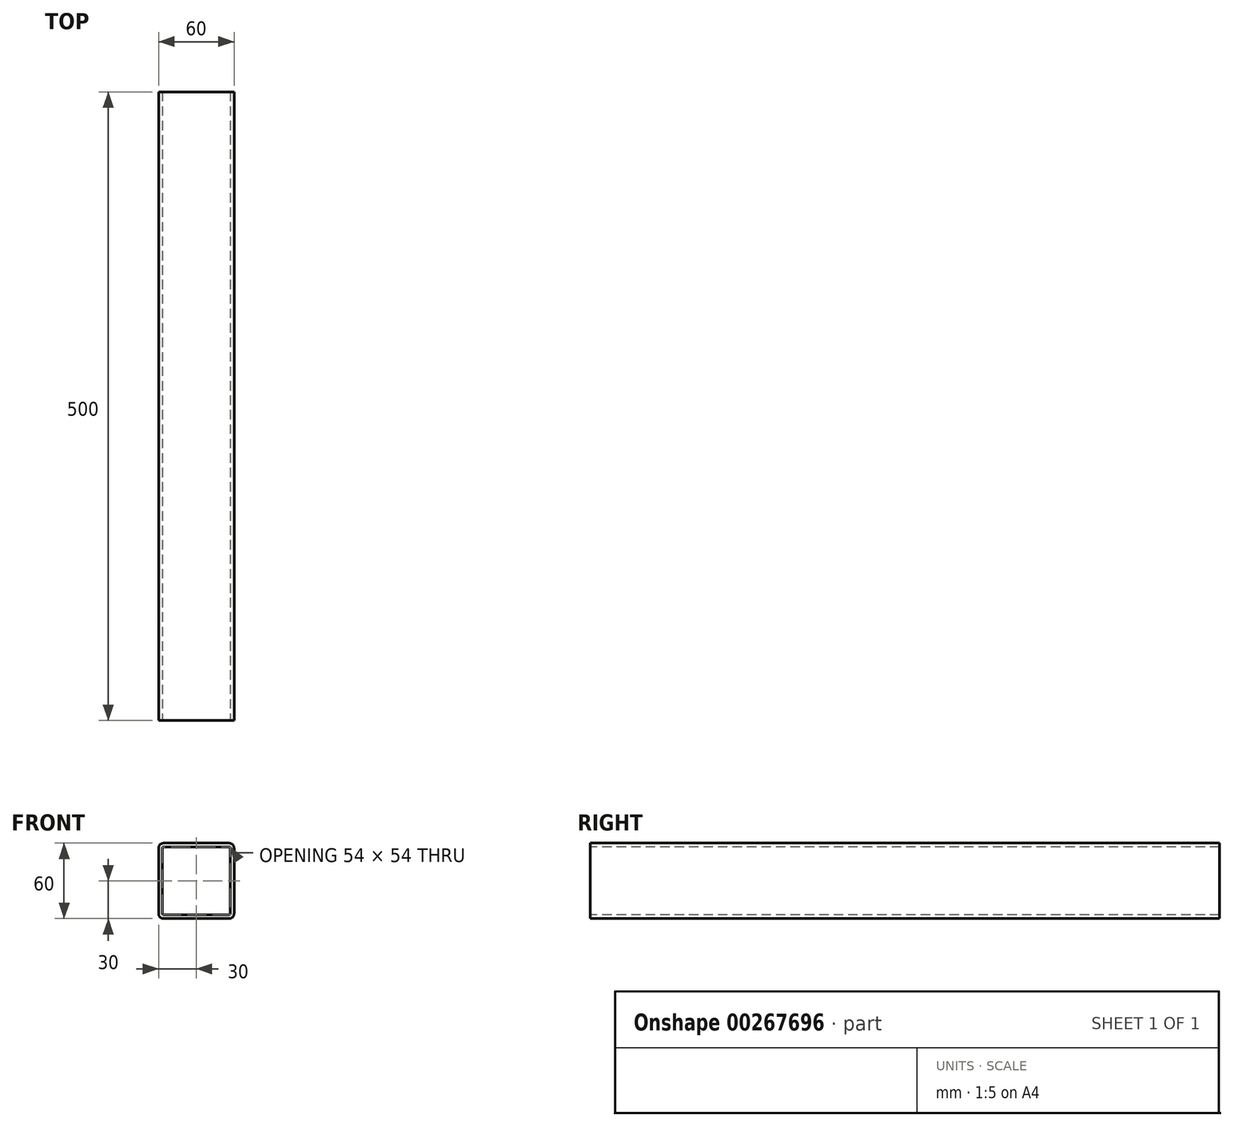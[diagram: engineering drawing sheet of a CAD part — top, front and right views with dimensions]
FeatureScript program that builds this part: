
annotation { "Feature Type Name" : "Feature", "Feature Type Description" : "" }
export const myFeature = defineFeature(function(context is Context, id is Id, definition is map)
    precondition{}
    {
        {
            var Q0;
            Q0=qCreatedBy(makeId("Front.planeOp"),FACE);
            var sketch = newSketch(context, id + "F0", { "sketchPlane" : qUnion([Q0])});
            skLineSegment(sketch, "E0.bottom", {"start": v(26, -30) * mm, "end": v(-26, -30) * mm});
            skLineSegment(sketch, "E0.top", {"start": v(26, 30) * mm, "end": v(-26, 30) * mm});
            skLineSegment(sketch, "E0.left", {"start": v(30, -26) * mm, "end": v(30, 26) * mm});
            skLineSegment(sketch, "E0.right", {"start": v(-30, -26) * mm, "end": v(-30, 26) * mm});
            skPoint(sketch, "E0.middle", {"position": v(0, 0) * mm});
            skPoint(sketch, "E1.visualSharp", {"position": v(-30, 30) * mm});
            skArc(sketch, "E1.filletArc", {"start": v(-26, 30) * mm, "mid": v(-28.83, 28.83) * mm, "end": v(-30, 26) * mm});
            skPoint(sketch, "E2.visualSharp", {"position": v(30, 30) * mm});
            skArc(sketch, "E2.filletArc", {"start": v(30, 26) * mm, "mid": v(28.83, 28.83) * mm, "end": v(26, 30) * mm});
            skPoint(sketch, "E3.visualSharp", {"position": v(30, -30) * mm});
            skArc(sketch, "E3.filletArc", {"start": v(26, -30) * mm, "mid": v(28.83, -28.83) * mm, "end": v(30, -26) * mm});
            skPoint(sketch, "E4.visualSharp", {"position": v(-30, -30) * mm});
            skArc(sketch, "E4.filletArc", {"start": v(-30, -26) * mm, "mid": v(-28.83, -28.83) * mm, "end": v(-26, -30) * mm});
            skArc(sketch, "E5.0", {"start": v(-27, -26) * mm, "mid": v(-26.7, -26.7) * mm, "end": v(-26, -27) * mm});
            skLineSegment(sketch, "E5.1", {"start": v(26, -27) * mm, "end": v(-26, -27) * mm});
            skLineSegment(sketch, "E5.2", {"start": v(-27, -26) * mm, "end": v(-27, 26) * mm});
            skArc(sketch, "E5.3", {"start": v(26, -27) * mm, "mid": v(26.7, -26.7) * mm, "end": v(27, -26) * mm});
            skArc(sketch, "E5.4", {"start": v(-26, 27) * mm, "mid": v(-26.7, 26.7) * mm, "end": v(-27, 26) * mm});
            skLineSegment(sketch, "E5.5", {"start": v(26, 27) * mm, "end": v(-26, 27) * mm});
            skArc(sketch, "E5.6", {"start": v(27, 26) * mm, "mid": v(26.7, 26.7) * mm, "end": v(26, 27) * mm});
            skLineSegment(sketch, "E5.7", {"start": v(27, -26) * mm, "end": v(27, 26) * mm});
            skSolve(sketch);
        }
        {
            var Q0;
            Q0=qSketchRegion(id+"F0",true);
            extrude(context, id + "F1", {"entities" : qUnion([Q0]), "oppositeDirection" : true, "depth" : 500 * mm});
        }
    });
